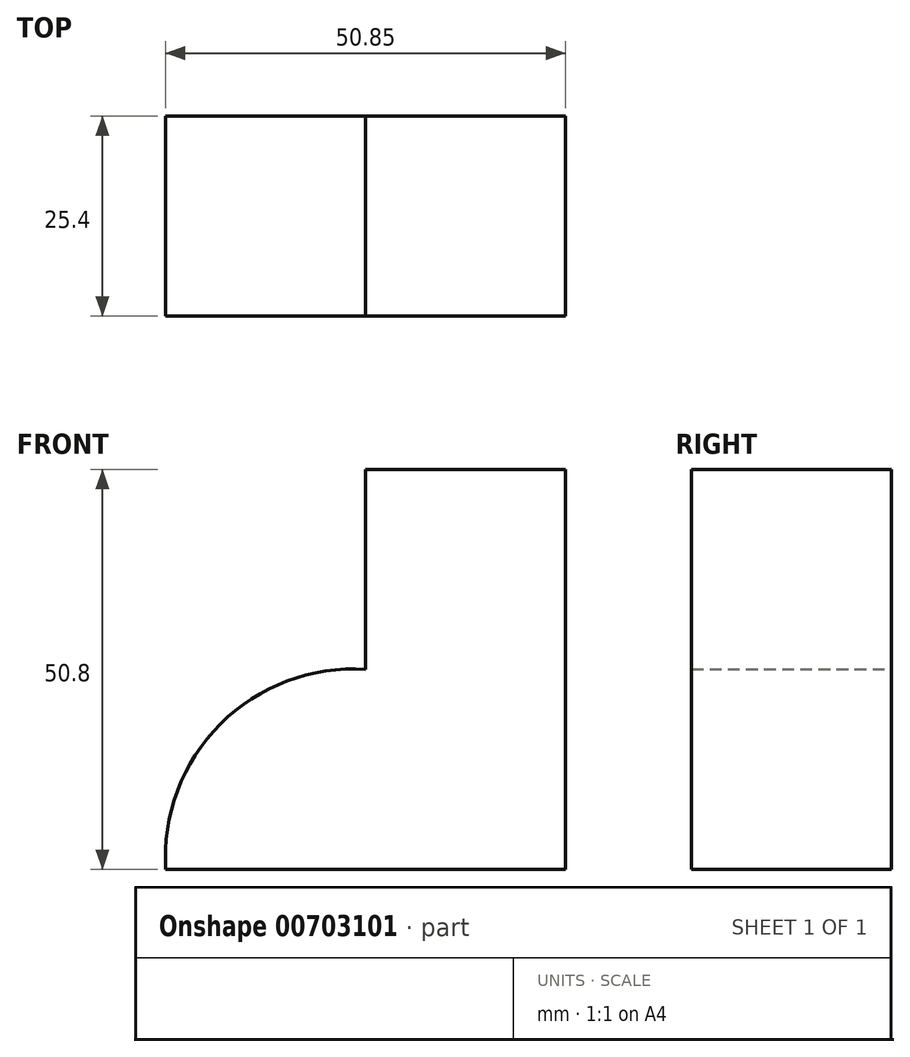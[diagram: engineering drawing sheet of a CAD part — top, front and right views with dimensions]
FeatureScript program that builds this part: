
annotation { "Feature Type Name" : "Feature", "Feature Type Description" : "" }
export const myFeature = defineFeature(function(context is Context, id is Id, definition is map)
    precondition{}
    {
        {
            var Q0;
            Q0=qCreatedBy(makeId("Front.planeOp"),FACE);
            var sketch = newSketch(context, id + "F0", { "sketchPlane" : qUnion([Q0])});
            skLineSegment(sketch, "E0", {"start": v(-41.72, 29.88) * mm, "end": v(-16.32, 29.88) * mm});
            skLineSegment(sketch, "E1", {"start": v(-16.32, 29.88) * mm, "end": v(-16.32, -20.92) * mm});
            skLineSegment(sketch, "E2", {"start": v(-16.32, -20.92) * mm, "end": v(-67.12, -20.92) * mm});
            skLineSegment(sketch, "E3", {"start": v(-41.72, 29.88) * mm, "end": v(-41.72, 4.48) * mm});
            skArc(sketch, "E4", {"start": v(-41.72, 4.48) * mm, "mid": v(-60.18, -2.45) * mm, "end": v(-67.12, -20.92) * mm});
            skSolve(sketch);
        }
        {
            var Q0;
            Q0=makeQuery(id+"F0.imprint","IMPRINT",FACE,{"disambiguationData":[TD([[makeQuery(id+"F0.imprint","IMPRINT",EDGE,{"derivedFrom":sQuery(id+"F0.wireOp",EDGE,"E0")}),-1.0]])]});
            extrude(context, id + "F1", {"entities" : qUnion([Q0]), "depth" : 25.4 * mm, "offsetDistance" : 25.4 * mm});
        }
    });
